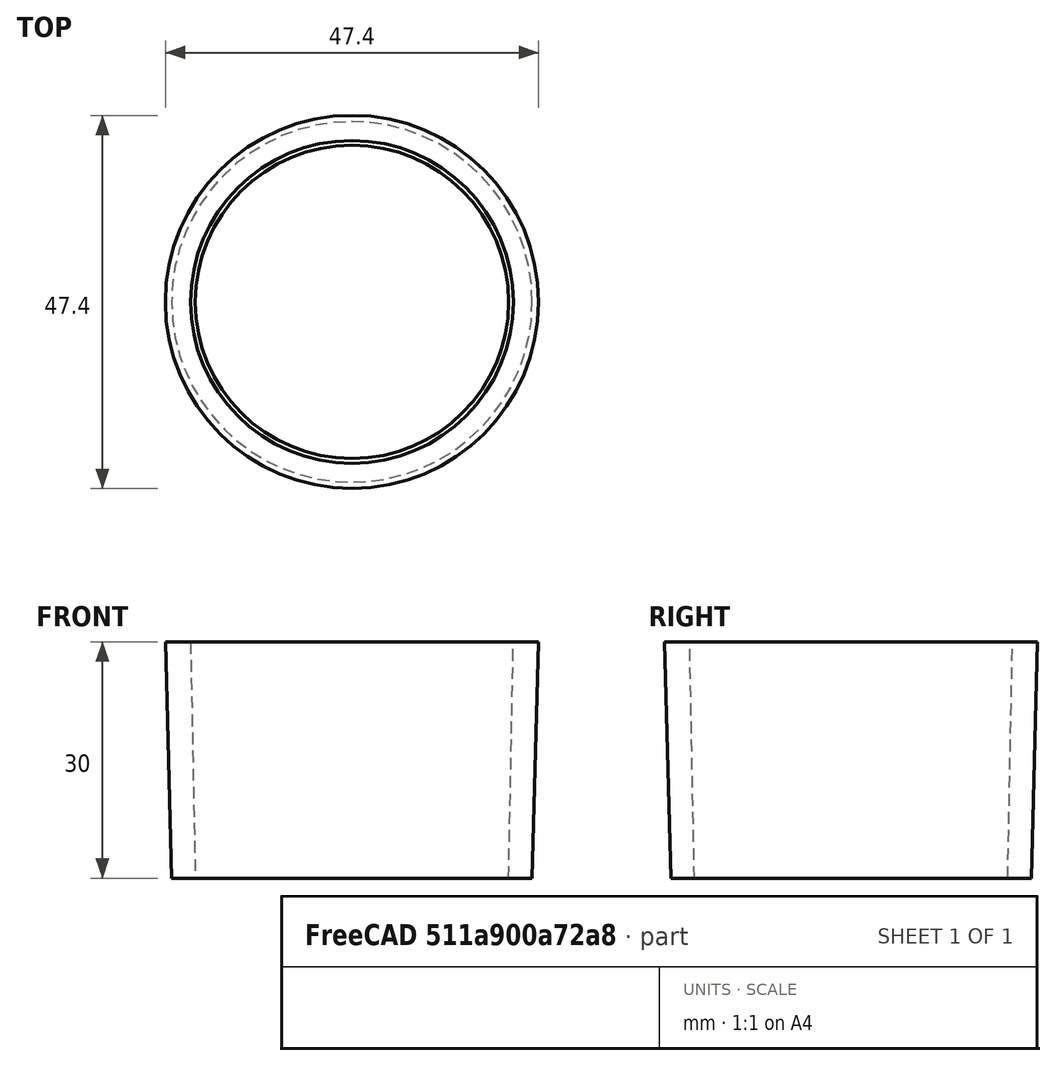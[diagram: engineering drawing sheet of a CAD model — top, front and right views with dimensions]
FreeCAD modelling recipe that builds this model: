
FCSTD DOCUMENT  (FreeCAD 1.1R39748 (Git))
Label: переходник
License: All rights reserved
LicenseURL: https://en.wikipedia.org/wiki/All_rights_reserved
objects: App::Point×1, Sketcher::SketchObject×1, PartDesign::Revolution×1, PartDesign::Body×1
note: 6 computed .brp shape members not serialized (recipe doc carries the construction recipe); baked Part::Feature solids carry a one-line shape summary decoded from their .brp

FEATURE [App::Point] Origin001
  Role = Origin
FEATURE [Sketcher::SketchObject] Sketch
  ArcFitTolerance = 1e-06
  AttachmentSupport = -> [XZ_Plane]
  ExternalTypes = [0]
  FullyConstrained = false
  MakeInternals = false
  MapMode = 5
  Placement = pos=(0,0,0) rot=(1,0,0;1.5708rad)
  expr: Constraints[1] = (50 - 1.8 * 2) / 2 - 0.3
  expr: Constraints[2] = (50 - 1.8 * 2) / 2 + 0.5
  sketch-geometry (6):
    g0: LineSegment StartX=-23.7 StartY=30 StartZ=0 EndX=-22.9 EndY=0 EndZ=0
    g1: GeomPoint X=0 Y=30 Z=0
    g2: LineSegment StartX=-22.9 StartY=0 StartZ=0 EndX=-22.9 EndY=0 EndZ=0
    g3: LineSegment StartX=-22.9 StartY=0 StartZ=0 EndX=-19.9 EndY=0 EndZ=0
    g4: LineSegment StartX=-20.5 StartY=30 StartZ=0 EndX=-19.9 EndY=0 EndZ=0
    g5: LineSegment StartX=-23.7 StartY=30 StartZ=0 EndX=-20.5 EndY=30 EndZ=0
  constraints (13):
    c: Horizontal(g0,g-1)
    c: Distance(g0,g-1) = 22.9
    c: DistanceX(g0,g-1) = 23.7
    c: PointOnObject(g1,g-2)
    c: Horizontal(g1,g0)
    c: DistanceY(g-1,g1) = 30
    c: PointOnObject(g2,g-1)
    c: Coincident(g3,g0)
    c: PointOnObject(g3,g-1)
    c: Distance(g3,g3) = 3
    c: Coincident(g5,g0)
    c: Coincident(g5,g4)
    c: Horizontal(g5)
FEATURE [PartDesign::Revolution] Revolution  label="В каналью"
  Angle = 360
  Angle2 = 60
  Axis = (0,2e-16,1)
  Base = (0,0,0)
  Placement = pos=(0,0,0) rot=(1,0,0;1.5708rad)
  Profile = -> Sketch
  ReferenceAxis = -> Sketch [V_Axis]
  Suppressed = false
  Type = 0
FEATURE [PartDesign::Body] Body  label="Тело"
  AllowCompound = false
  Group = -> [Sketch,Revolution]
  Origin = -> Origin
  Tip = -> Revolution
